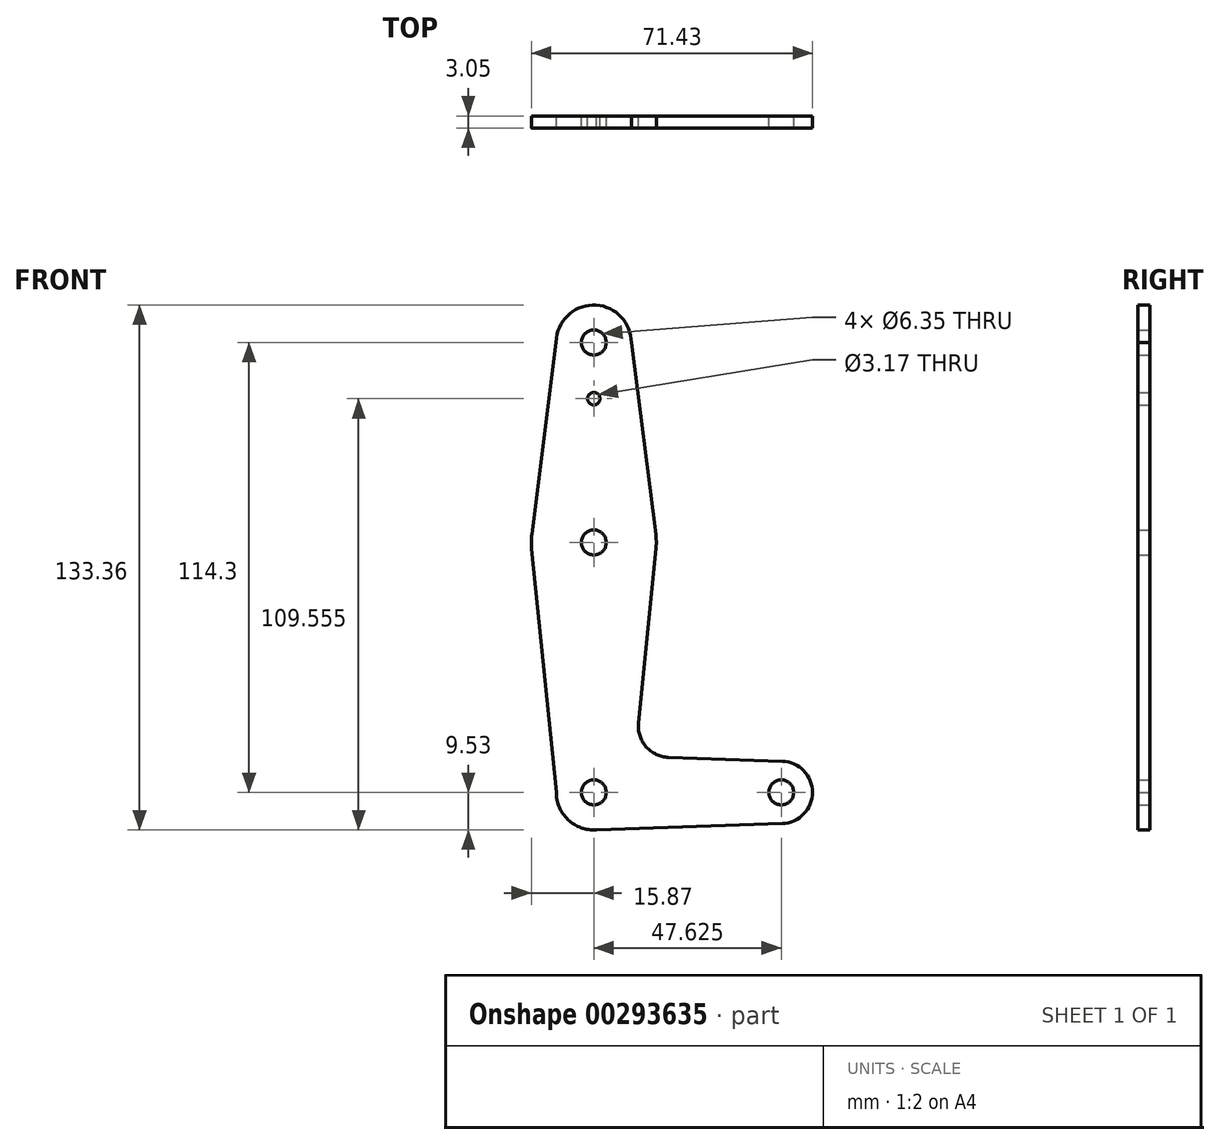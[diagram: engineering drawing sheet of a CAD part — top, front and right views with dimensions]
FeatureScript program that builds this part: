
annotation { "Feature Type Name" : "Feature", "Feature Type Description" : "" }
export const myFeature = defineFeature(function(context is Context, id is Id, definition is map)
    precondition{}
    {
        {
            var Q0;
            Q0=qCreatedBy(makeId("Front.planeOp"),FACE);
            var sketch = newSketch(context, id + "F0", { "sketchPlane" : qUnion([Q0])});
            skCircle(sketch, "E0", {"center": v(0, 0) * mm, "radius": 9.53 * mm});
            skCircle(sketch, "E1", {"center": v(0, 63.5) * mm, "radius": 15.88 * mm});
            skCircle(sketch, "E2", {"center": v(0, 114.3) * mm, "radius": 9.53 * mm});
            skCircle(sketch, "E3", {"center": v(47.62, 0) * mm, "radius": 7.94 * mm});
            skLineSegment(sketch, "E4", {"start": v(3.18, 0) * mm, "end": v(47.62, 0) * mm, "construction": true});
            skCircle(sketch, "E5", {"center": v(0, 114.3) * mm, "radius": 3.18 * mm});
            skCircle(sketch, "E6", {"center": v(0, 63.5) * mm, "radius": 3.18 * mm});
            skCircle(sketch, "E7", {"center": v(0, 0) * mm, "radius": 3.18 * mm});
            skCircle(sketch, "E8", {"center": v(47.62, 0) * mm, "radius": 3.18 * mm});
            skCircle(sketch, "E9", {"center": v(0, 100.03) * mm, "radius": 1.59 * mm});
            skLineSegment(sketch, "E10", {"start": v(9.52, 114.3) * mm, "end": v(15.75, 65.5) * mm});
            skLineSegment(sketch, "E11", {"start": v(-9.45, 115.5) * mm, "end": v(-15.75, 65.48) * mm});
            skLineSegment(sketch, "E12", {"start": v(0, -9.53) * mm, "end": v(47.89, -7.93) * mm});
            skLineSegment(sketch, "E13", {"start": v(0, 114.3) * mm, "end": v(0, 63.5) * mm, "construction": true});
            skLineSegment(sketch, "E14", {"start": v(0, 63.5) * mm, "end": v(0, 0) * mm, "construction": true});
            skLineSegment(sketch, "E15", {"start": v(15.8, 61.91) * mm, "end": v(11.35, 17.64) * mm});
            skLineSegment(sketch, "E16", {"start": v(19, 8.9) * mm, "end": v(47.89, 7.93) * mm});
            skPoint(sketch, "E17.newPointB", {"position": v(9.57, 0) * mm});
            skArc(sketch, "E17.filletArc", {"start": v(11.35, 17.64) * mm, "mid": v(13.27, 11.6) * mm, "end": v(19, 8.9) * mm});
            skLineSegment(sketch, "E18", {"start": v(-9.53, 0) * mm, "end": v(-15.8, 61.9) * mm});
            skSolve(sketch);
        }
        {
            var Q0;
            Q0 = qSketchRegion(id + "F0", true);
            extrude(context, id + "F1", {"entities" : qUnion([Q0]), "depth" : 3.05 * mm});
        }
    });
